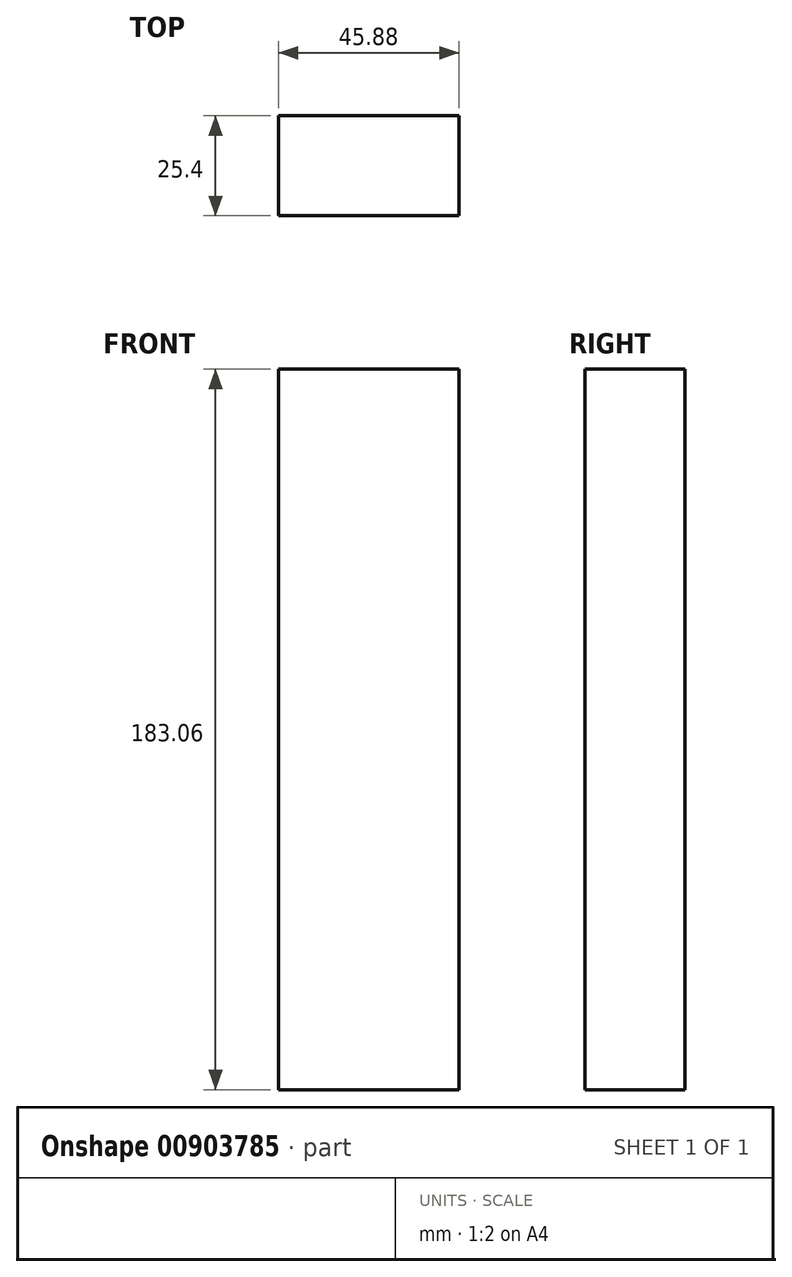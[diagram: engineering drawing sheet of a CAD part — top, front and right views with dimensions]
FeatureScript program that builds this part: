
annotation { "Feature Type Name" : "Feature", "Feature Type Description" : "" }
export const myFeature = defineFeature(function(context is Context, id is Id, definition is map)
    precondition{}
    {
        {
            var Q0;
            Q0=qCreatedBy(makeId("Front.planeOp"),FACE);
            var sketch = newSketch(context, id + "F0", { "sketchPlane" : qUnion([Q0])});
            skLineSegment(sketch, "E0.bottom", {"start": v(-22.94, 91.53) * mm, "end": v(22.94, 91.53) * mm});
            skLineSegment(sketch, "E0.top", {"start": v(-22.94, -91.53) * mm, "end": v(22.94, -91.53) * mm});
            skLineSegment(sketch, "E0.left", {"start": v(-22.94, 91.53) * mm, "end": v(-22.94, -91.53) * mm});
            skLineSegment(sketch, "E0.right", {"start": v(22.94, 91.53) * mm, "end": v(22.94, -91.53) * mm});
            skPoint(sketch, "E0.middle", {"position": v(0, 0) * mm});
            skSolve(sketch);
        }
        {
            var Q0;
            Q0=makeQuery(id+"F0.imprint","IMPRINT",FACE,{"disambiguationData":[TD([[makeQuery(id+"F0.imprint","IMPRINT",EDGE,{"derivedFrom":sQuery(id+"F0.wireOp",EDGE,"E0.bottom")}),-1.0]])]});
            extrude(context, id + "F1", {"entities" : qUnion([Q0]), "depth" : 25.4 * mm, "offsetDistance" : 25.4 * mm});
        }
    });
